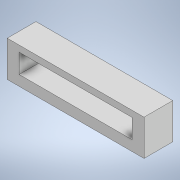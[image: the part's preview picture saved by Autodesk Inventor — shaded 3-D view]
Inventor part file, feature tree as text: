
AUTODESK INVENTOR PART (.ipt)
format: ipt  version: 2020 (Build 240168000, 168)  size: 149,504 bytes
history: native  units: mm
features: extrude x3, sketch x3
ambient origin geometry x8: Origin, YZ Plane, XZ Plane, XY Plane, X Axis, Y Axis, Z Axis, Center Point
bodies: Solid1 (feature_tree)
feature tree (6):
  extrude  "MainBody"  Depth=7.0mm
  extrude  "Clip1_Out"  Depth=7.0mm
  extrude  "Clip2_Out"  Depth=6.2mm TaperAngle=0.0deg
  sketch  "Sketch1"  dims[d0=33.3mm d1=7.0mm]
  sketch  "Sketch4"  dims[d3=0.0mm d5=7.0mm]
  sketch  "Sketch7"  dims[d6=0.0mm d7=6.2mm d8=0.0mm d9=1.5mm d10=13.85mm d11=0.0mm d14=7.0mm d15=2.9mm d16=0.0mm d22=1.5mm d23=7.0mm d26=13.65mm d27=0.0mm d34=27.5mm]
